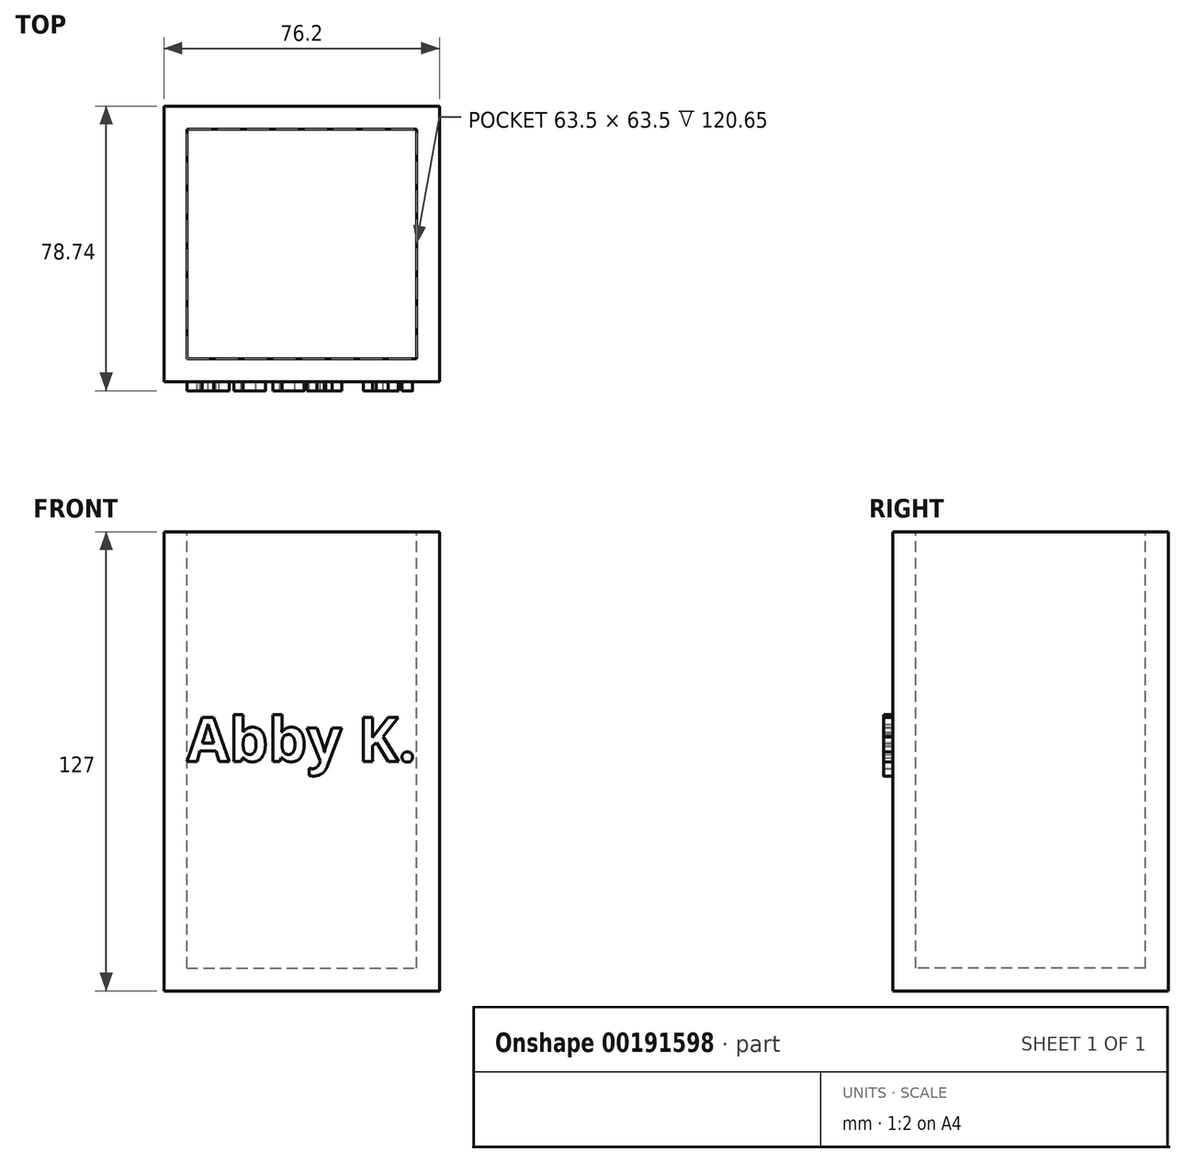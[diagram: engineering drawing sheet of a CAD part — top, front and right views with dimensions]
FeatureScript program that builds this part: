
annotation { "Feature Type Name" : "Feature", "Feature Type Description" : "" }
export const myFeature = defineFeature(function(context is Context, id is Id, definition is map)
    precondition{}
    {
        {
            var Q0;
            Q0=qCreatedBy(makeId("Front.planeOp"),FACE);
            var sketch = newSketch(context, id + "F0", { "sketchPlane" : qUnion([Q0])});
            skLineSegment(sketch, "E0.bottom", {"start": v(-27.47, 88.92) * mm, "end": v(48.73, 88.92) * mm});
            skLineSegment(sketch, "E0.top", {"start": v(-27.47, -38.08) * mm, "end": v(48.73, -38.08) * mm});
            skLineSegment(sketch, "E0.left", {"start": v(-27.47, 88.92) * mm, "end": v(-27.47, -38.08) * mm});
            skLineSegment(sketch, "E0.right", {"start": v(48.73, 88.92) * mm, "end": v(48.73, -38.08) * mm});
            skSolve(sketch);
        }
        {
            var Q0;
            Q0 = qSketchRegion(id + "F0", true);
            extrude(context, id + "F1", {"entities" : qUnion([Q0]), "depth" : 76.2 * mm});
        }
        {
            var Q0;
            Q0=makeQuery(id+"F1.opExtrude","SWEPT_FACE",FACE,{"disambiguationData":[OSD([sQuery(id+"F0.wireOp",EDGE,"E0.bottom")])]});
            var sketch = newSketch(context, id + "F2", { "sketchPlane" : qUnion([Q0])});
            skLineSegment(sketch, "E1.bottom", {"start": v(-21.12, -6.35) * mm, "end": v(42.38, -6.35) * mm});
            skLineSegment(sketch, "E1.top", {"start": v(-21.12, -69.85) * mm, "end": v(42.38, -69.85) * mm});
            skLineSegment(sketch, "E1.left", {"start": v(-21.12, -6.35) * mm, "end": v(-21.12, -69.85) * mm});
            skLineSegment(sketch, "E1.right", {"start": v(42.38, -6.35) * mm, "end": v(42.38, -69.85) * mm});
            skSolve(sketch);
        }
        {
            var Q0;
            Q0 = qSketchRegion(id + "F2", true);
            extrude(context, id + "F3", {"entities" : qUnion([Q0]), "operationType" : NewBodyOperationType.REMOVE, "oppositeDirection" : true, "depth" : 120.65 * mm});
        }
        {
            var Q0;
            Q0=makeQuery(id+"F1.opExtrude","CAP_FACE",FACE,{"disambiguationData":[OSD([sQuery(id+"F0.wireOp",EDGE,"E0.bottom"),sQuery(id+"F0.wireOp",EDGE,"E0.top"),sQuery(id+"F0.wireOp",EDGE,"E0.left"),sQuery(id+"F0.wireOp",EDGE,"E0.right")])],"isStart":false});
            var sketch = newSketch(context, id + "F4", { "sketchPlane" : qUnion([Q0])});
            skText(sketch, "E2", { "text": "Abby K.", "fontName": "OpenSans-Bold.ttf"});
            skPoint(sketch, "E2.secondSnap0", {"position": v(48.73, 25.42) * mm});
            const initialGuessF4  = {"E2": [-0.02112, 0.02542, 1, 0, 0.01222]};
            skSetInitialGuess(sketch, initialGuessF4);
            skSolve(sketch);
        }
        {
            var Q0;
            Q0 = qSketchRegion(id + "F4", true);
            extrude(context, id + "F5", {"entities" : qUnion([Q0]), "operationType" : NewBodyOperationType.ADD, "depth" : 2.54 * mm});
        }
    });
